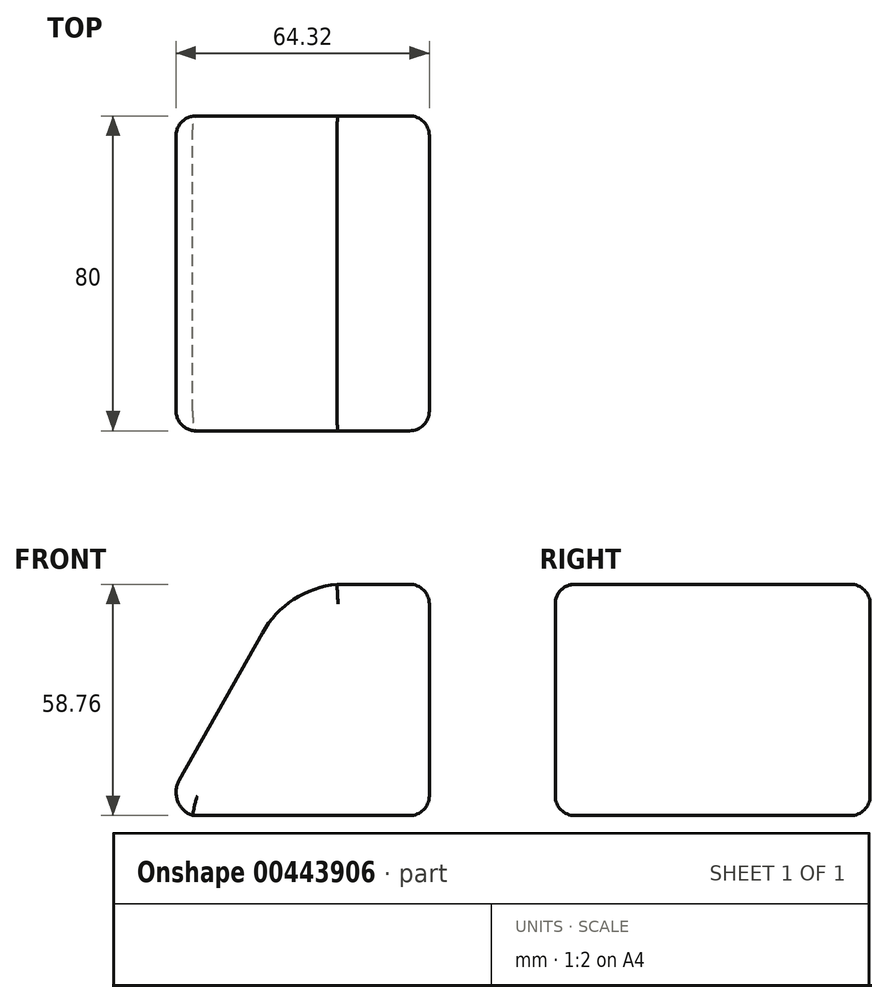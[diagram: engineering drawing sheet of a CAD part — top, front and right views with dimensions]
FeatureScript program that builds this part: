
annotation { "Feature Type Name" : "Feature", "Feature Type Description" : "" }
export const myFeature = defineFeature(function(context is Context, id is Id, definition is map)
    precondition{}
    {
        {
            var Q0;
            Q0=qCreatedBy(makeId("Front.planeOp"),FACE);
            var sketch = newSketch(context, id + "F0", { "sketchPlane" : qUnion([Q0])});
            skLineSegment(sketch, "E0", {"start": v(0, 5) * mm, "end": v(0, 53.76) * mm});
            skLineSegment(sketch, "E1", {"start": v(-5, 0) * mm, "end": v(-60.11, 0) * mm});
            skLineSegment(sketch, "E2", {"start": v(-5, 58.76) * mm, "end": v(-23.44, 58.76) * mm});
            skLineSegment(sketch, "E3", {"start": v(-63.51, 8.97) * mm, "end": v(-42.38, 46.44) * mm});
            skArc(sketch, "E4", {"start": v(-23.44, 58.76) * mm, "mid": v(-34.42, 54.92) * mm, "end": v(-42.38, 46.44) * mm});
            skArc(sketch, "E5", {"start": v(-63.51, 8.97) * mm, "mid": v(-63.91, 3.69) * mm, "end": v(-60.11, 0) * mm});
            skPoint(sketch, "E6.visualSharp", {"position": v(0, 0) * mm});
            skArc(sketch, "E6.filletArc", {"start": v(-5, 0) * mm, "mid": v(-1.46, 1.46) * mm, "end": v(0, 5) * mm});
            skPoint(sketch, "E7.visualSharp", {"position": v(0, 58.76) * mm});
            skArc(sketch, "E7.filletArc", {"start": v(0, 53.76) * mm, "mid": v(-1.46, 57.3) * mm, "end": v(-5, 58.76) * mm});
            skSolve(sketch);
        }
        {
            var Q0;
            Q0=qSketchRegion(id+"F0",true);
            extrude(context, id + "F1", {"entities" : qUnion([Q0]), "depth" : 80 * mm});
        }
        {
            var Q0;
            Q0=makeQuery(id+"F1.opExtrude","CAP_EDGE",EDGE,{"disambiguationData":[OSD([sQuery(id+"F0.wireOp",EDGE,"E4")])],"isStart":false});
            var Q1;
            Q1=makeQuery(id+"F1.opExtrude","CAP_EDGE",EDGE,{"disambiguationData":[OSD([sQuery(id+"F0.wireOp",EDGE,"E2")])],"isStart":false});
            var Q2;
            Q2=makeQuery(id+"F1.opExtrude","CAP_EDGE",EDGE,{"disambiguationData":[OSD([sQuery(id+"F0.wireOp",EDGE,"E7.filletArc")])],"isStart":false});
            var Q3;
            Q3=makeQuery(id+"F1.opExtrude","CAP_EDGE",EDGE,{"disambiguationData":[OSD([sQuery(id+"F0.wireOp",EDGE,"E0")])],"isStart":false});
            var Q4;
            Q4=makeQuery(id+"F1.opExtrude","CAP_EDGE",EDGE,{"disambiguationData":[OSD([sQuery(id+"F0.wireOp",EDGE,"E6.filletArc")])],"isStart":false});
            var Q5;
            Q5=makeQuery(id+"F1.opExtrude","CAP_EDGE",EDGE,{"disambiguationData":[OSD([sQuery(id+"F0.wireOp",EDGE,"E1")])],"isStart":false});
            var Q6;
            Q6=makeQuery(id+"F1.opExtrude","CAP_EDGE",EDGE,{"disambiguationData":[OSD([sQuery(id+"F0.wireOp",EDGE,"E5")])],"isStart":false});
            var Q7;
            Q7=makeQuery(id+"F1.opExtrude","CAP_EDGE",EDGE,{"disambiguationData":[OSD([sQuery(id+"F0.wireOp",EDGE,"E3")])],"isStart":false});
            fillet(context, id + "F2", {"entities" : qUnion([Q0, Q1, Q2, Q3, Q4, Q5, Q6, Q7]), "radius" : 5 * mm, "tangentPropagation" : true, "allowEdgeOverflow" : false});
        }
        {
            var Q0;
            Q0=makeQuery(id+"F1.opExtrude","CAP_EDGE",EDGE,{"disambiguationData":[OSD([sQuery(id+"F0.wireOp",EDGE,"E2")])],"isStart":true});
            var Q1;
            Q1=makeQuery(id+"F1.opExtrude","CAP_EDGE",EDGE,{"disambiguationData":[OSD([sQuery(id+"F0.wireOp",EDGE,"E4")])],"isStart":true});
            var Q2;
            Q2=makeQuery(id+"F1.opExtrude","CAP_EDGE",EDGE,{"disambiguationData":[OSD([sQuery(id+"F0.wireOp",EDGE,"E3")])],"isStart":true});
            var Q3;
            Q3=makeQuery(id+"F1.opExtrude","CAP_EDGE",EDGE,{"disambiguationData":[OSD([sQuery(id+"F0.wireOp",EDGE,"E5")])],"isStart":true});
            var Q4;
            Q4=makeQuery(id+"F1.opExtrude","CAP_FACE",FACE,{"disambiguationData":[OSD([sQuery(id+"F0.wireOp",EDGE,"E0"),sQuery(id+"F0.wireOp",EDGE,"E1"),sQuery(id+"F0.wireOp",EDGE,"E2"),sQuery(id+"F0.wireOp",EDGE,"E3"),sQuery(id+"F0.wireOp",EDGE,"E4"),sQuery(id+"F0.wireOp",EDGE,"E5"),sQuery(id+"F0.wireOp",EDGE,"E6.filletArc"),sQuery(id+"F0.wireOp",EDGE,"E7.filletArc")])],"isStart":true});
            var Q5;
            Q5=makeQuery(id+"F1.opExtrude","CAP_EDGE",EDGE,{"disambiguationData":[OSD([sQuery(id+"F0.wireOp",EDGE,"E6.filletArc")])],"isStart":true});
            var Q6;
            Q6=makeQuery(id+"F1.opExtrude","CAP_EDGE",EDGE,{"disambiguationData":[OSD([sQuery(id+"F0.wireOp",EDGE,"E0")])],"isStart":true});
            fillet(context, id + "F3", {"entities" : qUnion([Q0, Q1, Q2, Q3, Q4, Q5, Q6]), "radius" : 5 * mm, "tangentPropagation" : true, "allowEdgeOverflow" : false});
        }
    });
